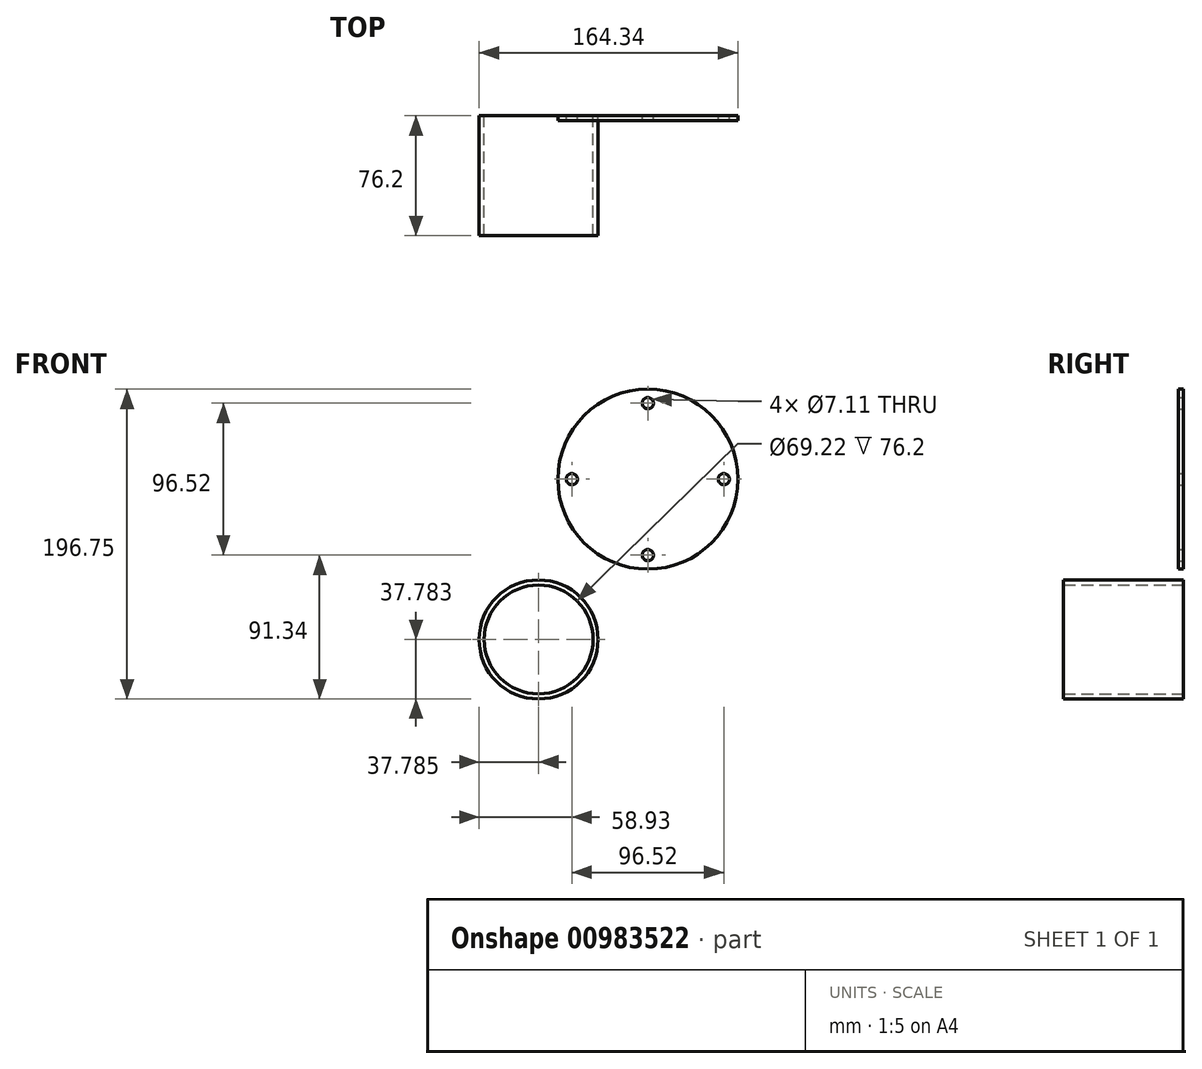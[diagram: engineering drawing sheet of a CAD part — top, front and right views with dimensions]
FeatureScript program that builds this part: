
annotation { "Feature Type Name" : "Feature", "Feature Type Description" : "" }
export const myFeature = defineFeature(function(context is Context, id is Id, definition is map)
    precondition{}
    {
        {
            var Q0;
            Q0=qCreatedBy(makeId("Front.planeOp"),FACE);
            var sketch = newSketch(context, id + "F0", { "sketchPlane" : qUnion([Q0])});
            skCircle(sketch, "E0", {"center": v(0, 0) * mm, "radius": 57.15 * mm});
            skCircle(sketch, "E1", {"center": v(-48.26, 0) * mm, "radius": 3.56 * mm});
            skCircle(sketch, "E2", {"center": v(48.26, 0) * mm, "radius": 3.56 * mm});
            skCircle(sketch, "E3", {"center": v(0, 48.26) * mm, "radius": 3.56 * mm});
            skCircle(sketch, "E4", {"center": v(0, -48.26) * mm, "radius": 3.56 * mm});
            skSolve(sketch);
        }
        {
            var Q0;
            Q0=makeQuery(id+"F0.imprint","IMPRINT",FACE,{"disambiguationData":[TD([[makeQuery(id+"F0.imprint","IMPRINT",EDGE,{"derivedFrom":sQuery(id+"F0.wireOp",EDGE,"CQ6ZLh3Z-gN7G-gAuD-24M7-dqEcXqA8SBAX")}),1.0]])]});
            var Q1;
            Q1=makeQuery(id+"F0.imprint","IMPRINT",FACE,{"disambiguationData":[TD([[makeQuery(id+"F0.imprint","IMPRINT",EDGE,{"derivedFrom":sQuery(id+"F0.wireOp",EDGE,"CQ6ZLh3Z-gN7G-gAuD-24M7-dqEcXqA8SBAX")}),-1.0]])]});
            var Q2;
            Q2=makeQuery(id+"F0.imprint","IMPRINT",FACE,{"disambiguationData":[TD([[makeQuery(id+"F0.imprint","IMPRINT",EDGE,{"derivedFrom":sQuery(id+"F0.wireOp",EDGE,"E0")}),1.0]])]});
            extrude(context, id + "F1", {"entities" : qUnion([Q0, Q1, Q2]), "depth" : 3.17 * mm, "offsetDistance" : 25.4 * mm});
        }
        {
            var Q0;
            Q0=qCreatedBy(makeId("Front.planeOp"),FACE);
            var sketch = newSketch(context, id + "F2", { "sketchPlane" : qUnion([Q0])});
            skCircle(sketch, "E5", {"center": v(-69.4, -101.82) * mm, "radius": 37.78 * mm});
            skCircle(sketch, "E6", {"center": v(-69.4, -101.82) * mm, "radius": 34.6 * mm});
            skSolve(sketch);
        }
        {
            var Q0;
            Q0=makeQuery(id+"F2.imprint","IMPRINT",FACE,{"disambiguationData":[TD([[makeQuery(id+"F2.imprint","IMPRINT",EDGE,{"derivedFrom":sQuery(id+"F2.wireOp",EDGE,"E5")}),1.0]])]});
            extrude(context, id + "F3", {"entities" : qUnion([Q0]), "depth" : 76.2 * mm, "offsetDistance" : 25.4 * mm});
        }
    });
